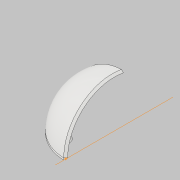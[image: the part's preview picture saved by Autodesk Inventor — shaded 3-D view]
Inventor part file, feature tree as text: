
AUTODESK INVENTOR PART (.ipt)
format: ipt  version: 2019.2 (Build 232265000, 265)  size: 646,144 bytes
history: native  units: mm
features: plane x17, sketch x9, extrude x7, other x6, fillet x5, revolve x3, chamfer x2, projected_geometry x2, mirror x1
ambient origin geometry x8: Origin, YZ Plane, XZ Plane, XY Plane, X Axis, Y Axis, Z Axis, Center Point
bodies: Volumenkörper1 (feature_tree)
feature tree (52):
  revolve  "Umdrehung1"
  sketch  "Skizze2"  dims[d2=90.0deg]
  sketch  "Skizze3"  dims[d3=1.0mm]
  plane  "Arbeitsebene1"
  revolve  "Umdrehung2"
  revolve  "Umdrehung3"
  other  "Arbeitsachse1"
  plane  "Arbeitsebene4"
  chamfer  "Fase6"  Distance=2.5mm Angle=45.0deg
  extrude  "Extrusion7"  Depth=4.0mm TaperAngle=0.0deg
  chamfer  "Fase11"  Distance=2.5mm Angle=45.0deg
  other  "Arbeitsachse5"
  plane  "Arbeitsebene21"
  plane  "Arbeitsebene20"
  plane  "Arbeitsebene25"
  other  "Arbeitspunkt3"
  plane  "Arbeitsebene27"
  plane  "Arbeitsebene28"
  plane  "Arbeitsebene31"
  plane  "Arbeitsebene34"
  other  "Trennen4"
  plane  "Arbeitsebene35"
  other  "Arbeitsachse8"
  sketch  "Skizze24"  dims[d5=180.0deg]
  extrude  "Extrusion16"  TaperAngle=90.0deg  [1 undecoded]
  extrude  "Extrusion17"  TaperAngle=0.0deg  [1 undecoded]
  fillet  "Rundung9"  [1 undecoded]
  mirror  "Spiegeln4"
  extrude  "Extrusion18"  TaperAngle=90.0deg  [1 undecoded]
  other  "Arbeitsachse9"
  extrude  "Extrusion19"  [1 undecoded]
  extrude  "Extrusion20"  Depth=4.0mm
  fillet  "Rundung10"  [1 undecoded]
  extrude  "Extrusion21"  [1 undecoded]
  fillet  "Rundung11"  [1 undecoded]
  fillet  "Rundung12"  Radius=5.0mm
  fillet  "Rundung13"  Radius=7.0mm
  sketch  "Skizze1"  dims[d1=123.0mm]
  sketch  "Skizze15"  dims[d4=3.0mm]
  projected_geometry  "Projizierte Kontur3"
  plane  "Arbeitsebene29"
  plane  "Arbeitsebene30"
  plane  "Arbeitsebene33"
  plane  "Arbeitsebene36"
  plane  "Arbeitsebene37"
  sketch  "Skizze25"  dims[d6=1.0mm]
  plane  "Arbeitsebene38"
  plane  "Arbeitsebene39"
  sketch  "Skizze26"  dims[d7=2.0mm]
  sketch  "Skizze27"  dims[d8=180.0deg]
  projected_geometry  "Projizierte Kontur7"
  sketch  "Skizze28"  dims[d10=-61.0mm d42=2.5mm d43=2.0mm d44=45.0deg d97=2.5mm d98=0.0mm d99=2.5mm d100=2.0mm d101=45.0deg d102=90.0deg d103=0.0mm d116=-59.0mm d117=90.0deg d118=-52.0mm d119=-20.0mm d133=50.0mm d147=45.0deg d148=-14.5mm d149=-8.5mm d150=5.0mm d151=7.0mm d152=3.25mm d153=10.0mm d154=0.0mm d155=3.5mm d156=0.0mm d157=3.5mm d158=2.1mm d159=18.25mm d160=0.0mm d161=-44.0mm d162=-32.0mm d163=6.0mm d164=0.5mm d165=8.0mm d166=10.0mm d167=0.0mm d168=4.0mm d169=0.0mm d170=4.0mm d171=2.1mm d172=4.0mm d173=0.0mm d174=0.25mm d175=0.25mm d176=0.25mm]
note: 8 required parameter values undecoded (feature->parameter linkage not recoverable at this tier; creation-order binding heuristic only, values carry confidence <= 0.55)
